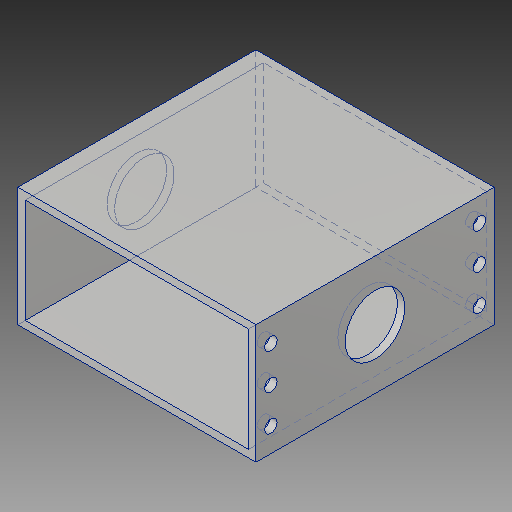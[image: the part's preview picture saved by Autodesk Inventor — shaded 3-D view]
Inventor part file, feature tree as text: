
AUTODESK INVENTOR PART (.ipt)
format: ipt  version: 2019 (Build 230136000, 136)  size: 137,728 bytes
history: native  units: in
note: dims shown in document units (in); Inventor stores cm internally (conversion verified against a paired STEP export)
features: extrude x3, sketch x3
ambient origin geometry x8: Origin, YZ Plane, XZ Plane, XY Plane, X Axis, Y Axis, Z Axis, Center Point
bodies: Solid1 (feature_tree)
feature tree (6):
  extrude  "Extrusion1"  Depth=0.125in
  extrude  "Extrusion3"  Depth=4.0in
  extrude  "Extrusion4"  Depth=0.125in
  sketch  "Sketch1"  dims[d0=2.0in d1=0.125in]
  sketch  "Sketch2"  dims[d2=4.0in d3=0.0in d4=0.21in]
  sketch  "Sketch3"  dims[d5=0.25in d6=0.6in d9=1.0in d10=0.0in d11=4.0in d12=0.125in d13=1.0in d14=1.0in d15=0.0in]
